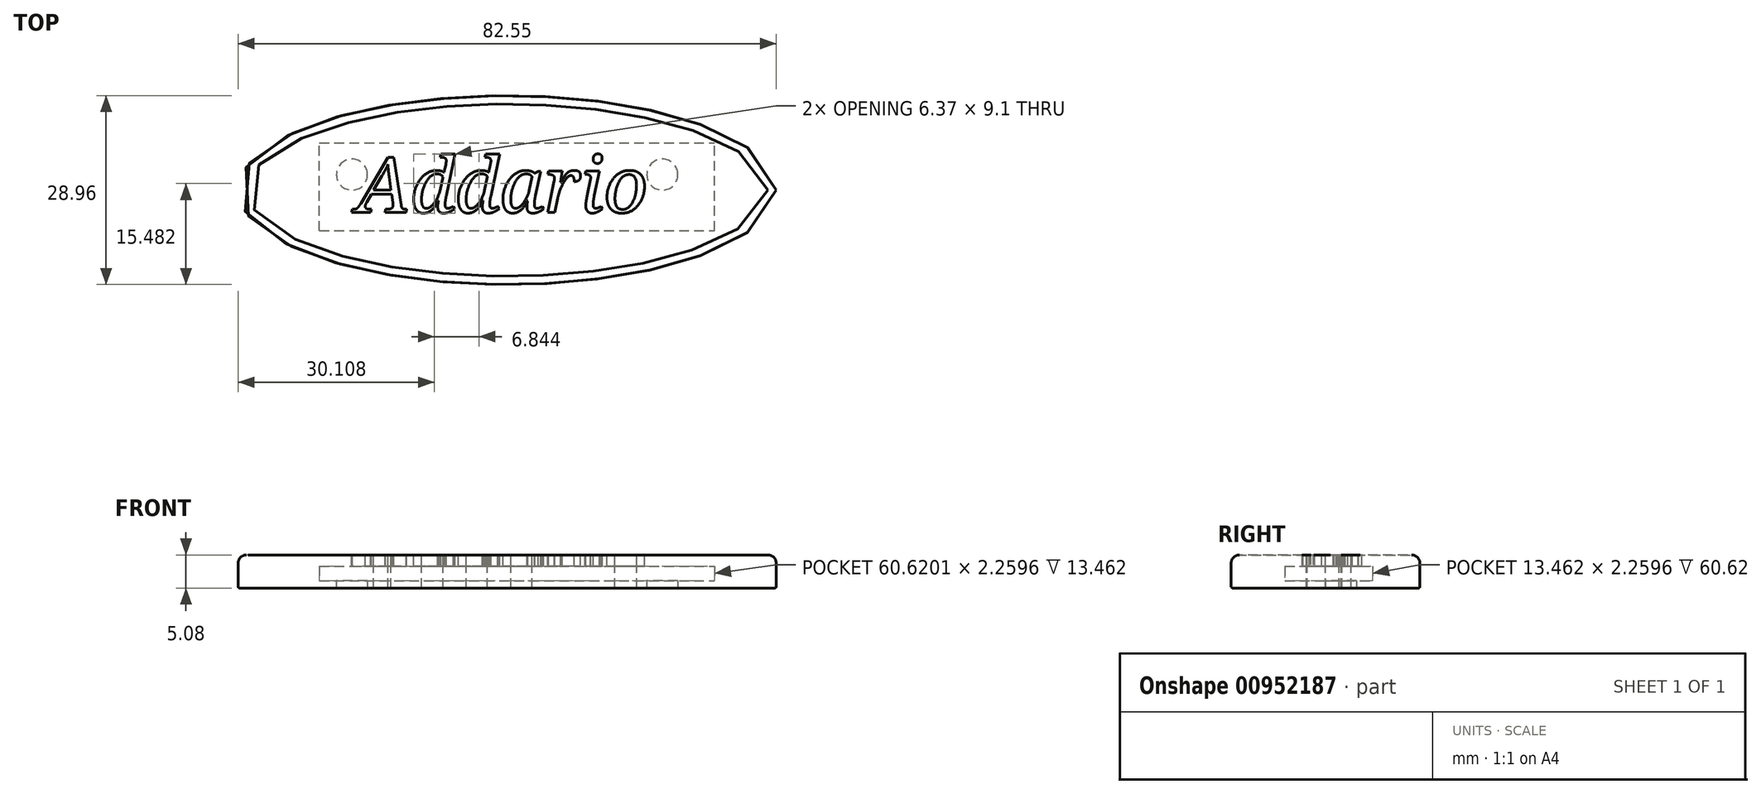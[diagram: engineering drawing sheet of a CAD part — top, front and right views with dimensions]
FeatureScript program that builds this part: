
annotation { "Feature Type Name" : "Feature", "Feature Type Description" : "" }
export const myFeature = defineFeature(function(context is Context, id is Id, definition is map)
    precondition{}
    {
        {
            var Q0;
            Q0=qCreatedBy(makeId("Top.planeOp"),FACE);
            var sketch = newSketch(context, id + "F0", { "sketchPlane" : qUnion([Q0])});
            skEllipse(sketch, "E0", {"center": v(0, 0) * mm, "majorRadius": 41.28 * mm, "minorRadius": 14.48 * mm, "majorAxis": v(1, 0)});
            skPoint(sketch, "E1.centerSnap0", {"position": v(-41.28, 0) * mm});
            skCircle(sketch, "E2", {"center": v(23.81, 2.38) * mm, "radius": 2.38 * mm});
            skPoint(sketch, "E2.centerSnap0", {"position": v(41.28, 0) * mm});
            skCircle(sketch, "E3", {"center": v(-23.81, 2.38) * mm, "radius": 2.38 * mm});
            skPoint(sketch, "E4", {"position": v(0, 14.48) * mm});
            skPoint(sketch, "E5", {"position": v(0, -14.48) * mm});
            skSolve(sketch);
        }
        {
            var Q0;
            Q0=makeQuery(id+"F0.imprint","IMPRINT",FACE,{"disambiguationData":[TD([[makeQuery(id+"F0.imprint","IMPRINT",EDGE,{"derivedFrom":sQuery(id+"F0.wireOp",EDGE,"E0")}),1.0]])]});
            var Q1;
            Q1=makeQuery(id+"F0.imprint","IMPRINT",FACE,{"disambiguationData":[TD([[makeQuery(id+"F0.imprint","IMPRINT",EDGE,{"derivedFrom":sQuery(id+"F0.wireOp",EDGE,"E3")}),1.0]])]});
            var Q2;
            Q2=makeQuery(id+"F0.imprint","IMPRINT",FACE,{"disambiguationData":[TD([[makeQuery(id+"F0.imprint","IMPRINT",EDGE,{"derivedFrom":sQuery(id+"F0.wireOp",EDGE,"E2")}),1.0]])]});
            extrude(context, id + "F1", {"entities" : qUnion([Q0, Q1, Q2]), "depth" : 5.08 * mm, "offsetDistance" : 25.4 * mm});
        }
        {
            var Q0;
            Q0=makeQuery(id+"F1.opExtrude","CAP_EDGE",EDGE,{"disambiguationData":[OSD([sQuery(id+"F0.wireOp",EDGE,"E0")])],"isStart":false});
            fillet(context, id + "F2", {"entities" : qUnion([Q0]), "radius" : 1.27 * mm, "tangentPropagation" : true, "allowEdgeOverflow" : false});
        }
        {
            var Q0;
            Q0=makeQuery(id+"F1.opExtrude","CAP_FACE",FACE,{"disambiguationData":[OSD([sQuery(id+"F0.wireOp",EDGE,"E0")])],"isStart":false});
            var sketch = newSketch(context, id + "F3", { "sketchPlane" : qUnion([Q0])});
            skText(sketch, "E6", { "text": "Addario", "fontName": "NotoSerif-Italic.ttf"});
            const initialGuessF3  = {"E6": [-0.02319, -0.00343, 1, 0, 0.00851]};
            skSetInitialGuess(sketch, initialGuessF3);
            skSolve(sketch);
        }
        {
            var Q0;
            Q0=qSketchRegion(id+"F3",true);
            extrude(context, id + "F4", {"entities" : qUnion([Q0]), "operationType" : NewBodyOperationType.REMOVE, "oppositeDirection" : true, "depth" : 2.54 * mm, "offsetDistance" : 25.4 * mm});
        }
        {
            var Q0;
            Q0=makeQuery(id+"F0.imprint","IMPRINT",FACE,{"disambiguationData":[TD([[makeQuery(id+"F0.imprint","IMPRINT",EDGE,{"derivedFrom":sQuery(id+"F0.wireOp",EDGE,"E3")}),1.0]])]});
            var Q1;
            Q1=makeQuery(id+"F0.imprint","IMPRINT",FACE,{"disambiguationData":[TD([[makeQuery(id+"F0.imprint","IMPRINT",EDGE,{"derivedFrom":sQuery(id+"F0.wireOp",EDGE,"E2")}),1.0]])]});
            var Q2;
            Q2=sQuery(id+"F0.wireOp",EDGE,"E3");
            var Q3;
            Q3=sQuery(id+"F0.wireOp",EDGE,"E2");
            extrude(context, id + "F5", {"entities" : qUnion([Q0, Q1]), "operationType" : NewBodyOperationType.REMOVE, "surfaceEntities" : qUnion([Q2, Q3]), "depth" : 2.54 * mm, "offsetDistance" : 25.4 * mm});
        }
        {
            var Q0;
            Q0=makeQuery(id+"F1.opExtrude","CAP_EDGE",EDGE,{"disambiguationData":[OSD([sQuery(id+"F0.wireOp",EDGE,"E0")])],"isStart":true});
            fillet(context, id + "F6", {"entities" : qUnion([Q0]), "radius" : 0.25 * mm, "tangentPropagation" : true, "allowEdgeOverflow" : false});
        }
        {
            var Q0;
            Q0=sQuery(id+"F0.wireOp",VERTEX,"E0.center");
            var Q1;
            Q1=sQuery(id+"F0.wireOp",VERTEX,"E4");
            cPlane(context, id + "F7", {"entities" : qUnion([Q0, Q1]), "cplaneType" : CPlaneType.MID_PLANE, "offset" : 25.4 * mm, "width" : 152.4 * mm, "height" : 152.4 * mm});
        }
        {
            var Q0;
            Q0=qCreatedBy(id+"F7.planeOp",FACE);
            var sketch = newSketch(context, id + "F8", { "sketchPlane" : qUnion([Q0])});
            skLineSegment(sketch, "E7.bottom", {"start": v(28.81, 3.37) * mm, "end": v(-31.8, 3.37) * mm});
            skLineSegment(sketch, "E7.top", {"start": v(28.81, 1.1) * mm, "end": v(-31.8, 1.1) * mm});
            skLineSegment(sketch, "E7.left", {"start": v(28.81, 3.37) * mm, "end": v(28.81, 1.1) * mm});
            skLineSegment(sketch, "E7.right", {"start": v(-31.8, 3.37) * mm, "end": v(-31.8, 1.1) * mm});
            skSolve(sketch);
        }
        {
            var Q0;
            Q0=qSketchRegion(id+"F8",true);
            extrude(context, id + "F9", {"entities" : qUnion([Q0]), "operationType" : NewBodyOperationType.REMOVE, "oppositeDirection" : true, "depth" : 13.46 * mm, "offsetDistance" : 25.4 * mm});
        }
        {
            var Q0;
            Q0=makeQuery(id+"F3.imprint","IMPRINT",FACE,{"disambiguationData":[TD([[makeQuery(id+"F3.imprint","IMPRINT",EDGE,{"derivedFrom":sQuery(id+"F3.wireOp",EDGE,"E6.sketch_text.stroke-24")}),1.0]])]});
            var Q1;
            Q1=makeQuery(id+"F3.imprint","IMPRINT",FACE,{"disambiguationData":[TD([[makeQuery(id+"F3.imprint","IMPRINT",EDGE,{"derivedFrom":sQuery(id+"F3.wireOp",EDGE,"E6.sketch_text.stroke-51")}),1.0]])]});
            var Q2;
            Q2=makeQuery(id+"F3.imprint","IMPRINT",FACE,{"disambiguationData":[TD([[makeQuery(id+"F3.imprint","IMPRINT",EDGE,{"derivedFrom":sQuery(id+"F3.wireOp",EDGE,"E6.sketch_text.stroke-80")}),1.0]])]});
            var Q3;
            Q3=makeQuery(id+"F3.imprint","IMPRINT",FACE,{"disambiguationData":[TD([[makeQuery(id+"F3.imprint","IMPRINT",EDGE,{"derivedFrom":sQuery(id+"F3.wireOp",EDGE,"E6.sketch_text.stroke-104")}),1.0]])]});
            var Q4;
            Q4=makeQuery(id+"F3.imprint","IMPRINT",FACE,{"disambiguationData":[TD([[makeQuery(id+"F3.imprint","IMPRINT",EDGE,{"derivedFrom":sQuery(id+"F3.wireOp",EDGE,"E6.sketch_text.stroke-157")}),1.0]])]});
            extrude(context, id + "F10", {"entities" : qUnion([Q0, Q1, Q2, Q3, Q4]), "oppositeDirection" : true, "depth" : 5.08 * mm, "offsetDistance" : 25.4 * mm});
        }
    });
